# Revit family: Insulation_Board_TimberHP
name_source: partatom
category: Generic Models
units: mm (PartAtom-declared; Revit-internal decimal feet)

## family parameters
Can host rebar = No
Cut with Voids When Loaded = Yes
Host = Face
Maintain Annotation Orientation = No
Part Type = Normal
Room Calculation Point = No
Round Connector Dimension = Use Diameter
Shared = No

## types (18) — shared parameters
CAD Details = https://www.arcat.com
Cut Groove = Yes
Cut Tongue = Yes
Default Elevation = 4' - 0"
Keynote = 07 21 00
Length = 8' - 0"
Manufacturer = TimberHP
Model = TimberBoard
Product Page URL = https://www.arcat.com
Specification = https://www.arcat.com
Top and bottom Flat = Yes
URL = https://timberhp.com

## per-type parameters (varying)
| type | Groove | Thickness | Tongue | Width |
| TimberBoard_1" (R3.6)x24"x8' | 0' - 0 11/32" | 0' - 1" | 0' - 0 11/32" | 2' - 0" |
| TimberBoard_1" (R3.6)x48"x8' | 0' - 0 11/32" | 0' - 1" | 0' - 0 11/32" | 4' - 0" |
| TimberBoard_1.5" (R5+)x48"x8' | 0' - 0 1/2" | 0' - 1 1/2" | 0' - 0 1/2" | 4' - 0" |
| TimberBoard_1.5" (R5+)x24"x8' | 0' - 0 1/2" | 0' - 1 1/2" | 0' - 0 1/2" | 2' - 0" |
| TimberBoard_2” (R7)x24"x8' | 0' - 0 21/32" | 0' - 2" | 0' - 0 21/32" | 2' - 0" |
| TimberBoard_2” (R7)x48"x8' | 0' - 0 21/32" | 0' - 2" | 0' - 0 21/32" | 4' - 0" |
| TimberBoard_2.5”(R9)x48"x8' | 0' - 0 27/32" | 0' - 2 1/2" | 0' - 0 27/32" | 4' - 0" |
| TimberBoard_2.5”(R9)x24"x8' | 0' - 0 27/32" | 0' - 2 1/2" | 0' - 0 27/32" | 2' - 0" |
| TimberBoard_3.5” (R13)x48"x8' | 0' - 1 5/32" | 0' - 3 1/2" | 0' - 1 5/32" | 4' - 0" |
| TimberBoard_3.5” (R13)x24"x8' | 0' - 1 5/32" | 0' - 3 1/2" | 0' - 1 5/32" | 2' - 0" |
| TimberBoard_4” (R15)x24"x8' | 0' - 1 11/32" | 0' - 4" | 0' - 1 11/32" | 2' - 0" |
| TimberBoard_4” (R15)x12"x8' | 0' - 1 11/32" | 0' - 4" | 0' - 1 11/32" | 1' - 0" |
| TimberBoard_ 5.5” (R20)x24"x8' | 0' - 1 27/32" | 0' - 5 1/2" | 0' - 1 27/32" | 2' - 0" |
| TimberBoard_ 5.5” (R20)x48"x8' | 0' - 1 27/32" | 0' - 5 1/2" | 0' - 1 27/32" | 4' - 0" |
| Timberboard_7.25” (R26)x48"x8' | 0' - 2 13/32" | 0' - 7 1/4" | 0' - 2 13/32" | 4' - 0" |
| Timberboard_7.25” (R26)x24"x8' | 0' - 2 13/32" | 0' - 7 1/4" | 0' - 2 13/32" | 2' - 0" |
| TimberBoard_9.25” (R34)x48"x8' | 0' - 3 3/32" | 0' - 9 1/4" | 0' - 3 3/32" | 4' - 0" |
| TimberBoard_9.25” (R34)x24"x8' | 0' - 3 3/32" | 0' - 9 1/4" | 0' - 3 3/32" | 2' - 0" |

## geometry (parser evidence)
native form markers: Sweep x2
no freeform markers — native parametric forms only
